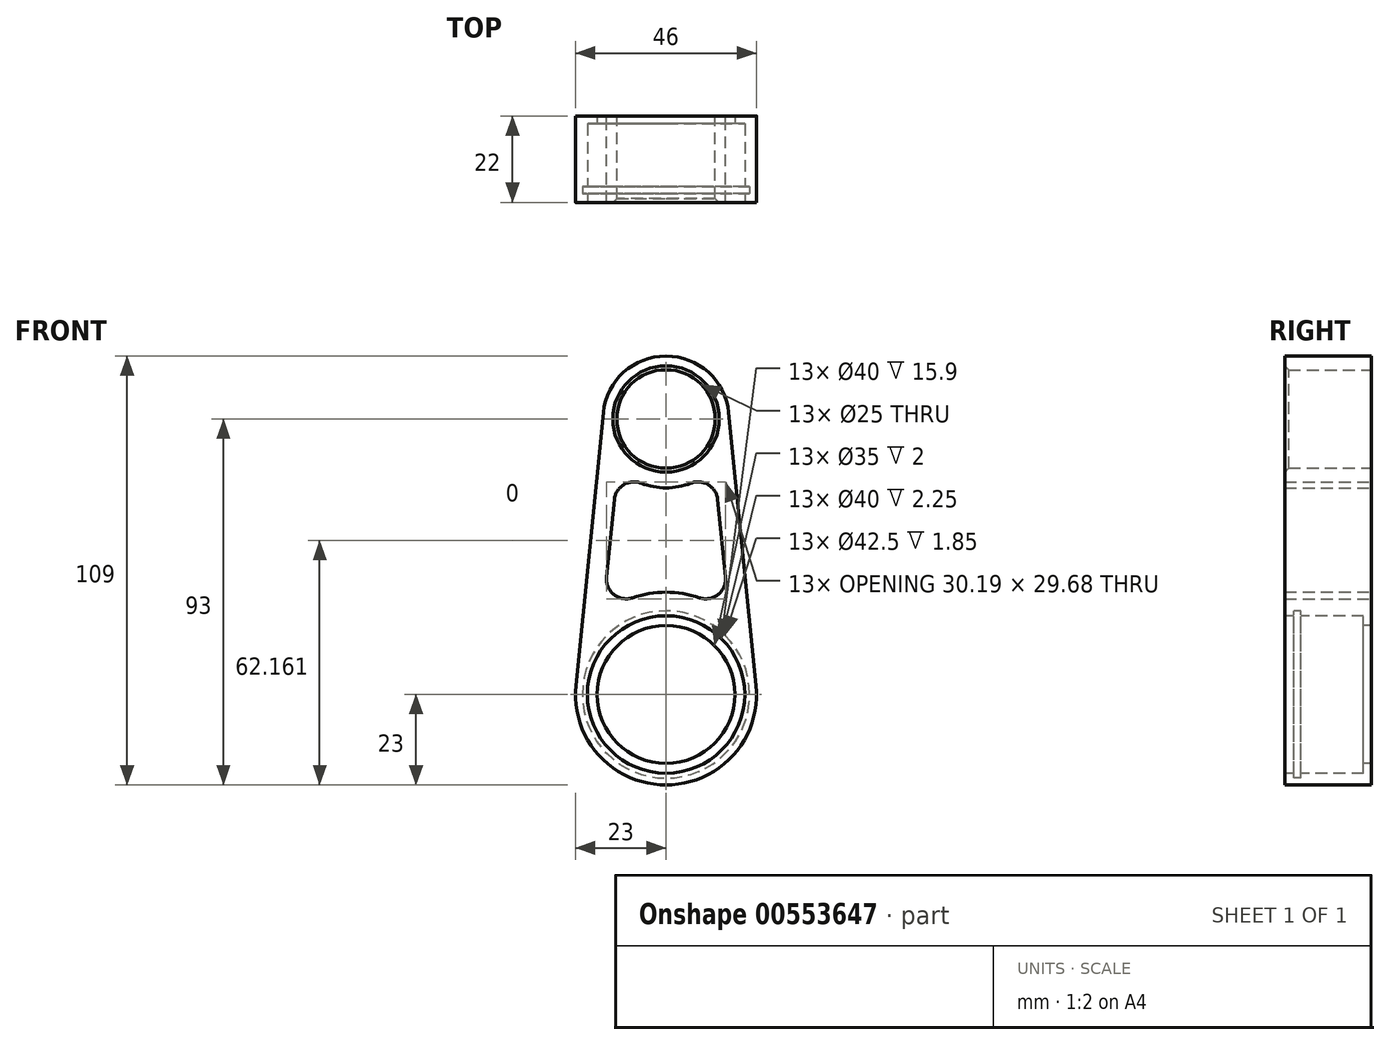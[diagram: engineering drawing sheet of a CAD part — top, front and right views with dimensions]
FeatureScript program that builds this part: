
annotation { "Feature Type Name" : "Feature", "Feature Type Description" : "" }
export const myFeature = defineFeature(function(context is Context, id is Id, definition is map)
    precondition{}
    {
        {
            var Q0;
            Q0=qCreatedBy(makeId("Front.planeOp"),FACE);
            var sketch = newSketch(context, id + "F0", { "sketchPlane" : qUnion([Q0])});
            skArc(sketch, "E0", {"start": v(-22.88, 2.3) * mm, "mid": v(0, -23) * mm, "end": v(22.88, 2.3) * mm});
            skArc(sketch, "E1", {"start": v(15.92, 71.6) * mm, "mid": v(0, 86) * mm, "end": v(-15.92, 71.6) * mm});
            skLineSegment(sketch, "E2", {"start": v(-15.92, 71.6) * mm, "end": v(-22.88, 2.3) * mm});
            skLineSegment(sketch, "E3", {"start": v(15.92, 71.6) * mm, "end": v(22.88, 2.3) * mm});
            skArc(sketch, "E4", {"start": v(-6.33, 53.68) * mm, "mid": v(0, 52.5) * mm, "end": v(6.33, 53.68) * mm});
            skArc(sketch, "E5", {"start": v(8.49, 24.58) * mm, "mid": v(0, 26) * mm, "end": v(-8.49, 24.58) * mm});
            skLineSegment(sketch, "E6", {"start": v(-13.11, 49.52) * mm, "end": v(-15.1, 29.8) * mm});
            skLineSegment(sketch, "E7", {"start": v(13.11, 49.52) * mm, "end": v(15.1, 29.8) * mm});
            skPoint(sketch, "E8.visualSharp", {"position": v(-12.3, 57.56) * mm});
            skArc(sketch, "E8.filletArc", {"start": v(-6.33, 53.68) * mm, "mid": v(-10.75, 53.29) * mm, "end": v(-13.11, 49.52) * mm});
            skPoint(sketch, "E9.visualSharp", {"position": v(12.3, 57.56) * mm});
            skArc(sketch, "E9.filletArc", {"start": v(13.11, 49.52) * mm, "mid": v(10.75, 53.29) * mm, "end": v(6.33, 53.68) * mm});
            skPoint(sketch, "E10.visualSharp", {"position": v(-16.03, 20.47) * mm});
            skArc(sketch, "E10.filletArc", {"start": v(-15.1, 29.8) * mm, "mid": v(-13.22, 25.38) * mm, "end": v(-8.49, 24.58) * mm});
            skPoint(sketch, "E11.visualSharp", {"position": v(16.03, 20.47) * mm});
            skArc(sketch, "E11.filletArc", {"start": v(8.49, 24.58) * mm, "mid": v(13.22, 25.38) * mm, "end": v(15.1, 29.8) * mm});
            skCircle(sketch, "E12", {"center": v(0, 70) * mm, "radius": 12.5 * mm});
            skSolve(sketch);
        }
        {
            var Q0;
            Q0 = qSketchRegion(id + "F0", true);
            extrude(context, id + "F1", {"entities" : qUnion([Q0]), "depth" : 22 * mm, "offsetDistance" : 25 * mm});
        }
        {
            var Q0;
            Q0=makeQuery(id+"F1.opExtrude","CAP_EDGE",EDGE,{"disambiguationData":[OSD([sQuery(id+"F0.wireOp",EDGE,"E12")])],"isStart":false});
            chamfer(context, id + "F2", {"entities" : qUnion([Q0]), "width" : 1 * mm, "tangentPropagation" : true});
        }
        {
            var Q0;
            Q0=makeQuery(id+"F1.opExtrude","CAP_FACE",FACE,{"disambiguationData":[OSD([sQuery(id+"F0.wireOp",EDGE,"E0"),sQuery(id+"F0.wireOp",EDGE,"E1"),sQuery(id+"F0.wireOp",EDGE,"E2"),sQuery(id+"F0.wireOp",EDGE,"E3"),sQuery(id+"F0.wireOp",EDGE,"E4"),sQuery(id+"F0.wireOp",EDGE,"E5"),sQuery(id+"F0.wireOp",EDGE,"E6"),sQuery(id+"F0.wireOp",EDGE,"E7"),sQuery(id+"F0.wireOp",EDGE,"E8.filletArc"),sQuery(id+"F0.wireOp",EDGE,"E9.filletArc"),sQuery(id+"F0.wireOp",EDGE,"E10.filletArc"),sQuery(id+"F0.wireOp",EDGE,"E11.filletArc"),sQuery(id+"F0.wireOp",EDGE,"E12")])],"isStart":false});
            var sketch = newSketch(context, id + "F3", { "sketchPlane" : qUnion([Q0])});
            skPoint(sketch, "E13", {"position": v(0, 0) * mm});
            skSolve(sketch);
        }
        {
            var Q0;
            Q0=sQuery(id+"F3.wireOp",VERTEX,"E13");
            var Q1;
            Q1=makeQuery(id+"F1.opExtrude","SWEPT_BODY",BODY,{"disambiguationData":[OSD([sQuery(id+"F0.wireOp",EDGE,"E0"),sQuery(id+"F0.wireOp",EDGE,"E1"),sQuery(id+"F0.wireOp",EDGE,"E2"),sQuery(id+"F0.wireOp",EDGE,"E3"),sQuery(id+"F0.wireOp",EDGE,"E4"),sQuery(id+"F0.wireOp",EDGE,"E5"),sQuery(id+"F0.wireOp",EDGE,"E6"),sQuery(id+"F0.wireOp",EDGE,"E7"),sQuery(id+"F0.wireOp",EDGE,"E8.filletArc"),sQuery(id+"F0.wireOp",EDGE,"E9.filletArc"),sQuery(id+"F0.wireOp",EDGE,"E10.filletArc"),sQuery(id+"F0.wireOp",EDGE,"E11.filletArc"),sQuery(id+"F0.wireOp",EDGE,"E12")])]});
            hole(context, id + "F4", {"style" : HoleStyle.C_BORE, "endStyle" : HoleEndStyle.THROUGH, "holeDiameter" : 35 * mm, "cBoreDiameter" : 40 * mm, "cBoreDepth" : 20 * mm, "isTappedThrough" : true, "tappedDepth" : 15.6 * mm, "tapClearance" : 3, "locations" : qUnion([Q0]), "scope" : qUnion([Q1])});
        }
        {
            var Q0;
            Q0=qCreatedBy(makeId("Right.planeOp"),FACE);
            var sketch = newSketch(context, id + "F5", { "sketchPlane" : qUnion([Q0])});
            skLineSegment(sketch, "E14.bottom", {"start": v(-17.9, 0) * mm, "end": v(-19.75, 0) * mm});
            skLineSegment(sketch, "E14.top", {"start": v(-17.9, 21.25) * mm, "end": v(-19.75, 21.25) * mm});
            skLineSegment(sketch, "E14.left", {"start": v(-17.9, 0) * mm, "end": v(-17.9, 21.25) * mm});
            skLineSegment(sketch, "E14.right", {"start": v(-19.75, 0) * mm, "end": v(-19.75, 21.25) * mm});
            skSolve(sketch);
        }
        {
            var Q0;
            Q0=makeQuery(id+"F5.imprint","IMPRINT",FACE,{"disambiguationData":[TD([[makeQuery(id+"F5.imprint","IMPRINT",EDGE,{"derivedFrom":sQuery(id+"F5.wireOp",EDGE,"E14.bottom")}),-1.0]])]});
            var Q1;
            Q1=sQuery(id+"F5.wireOp",EDGE,"E14.bottom");
            revolve(context, id + "F6", {"operationType" : NewBodyOperationType.REMOVE, "entities" : qUnion([Q0]), "axis" : qUnion([Q1]), "revolveType" : RevolveType.FULL, "oppositeDirection" : true});
        }
    });
